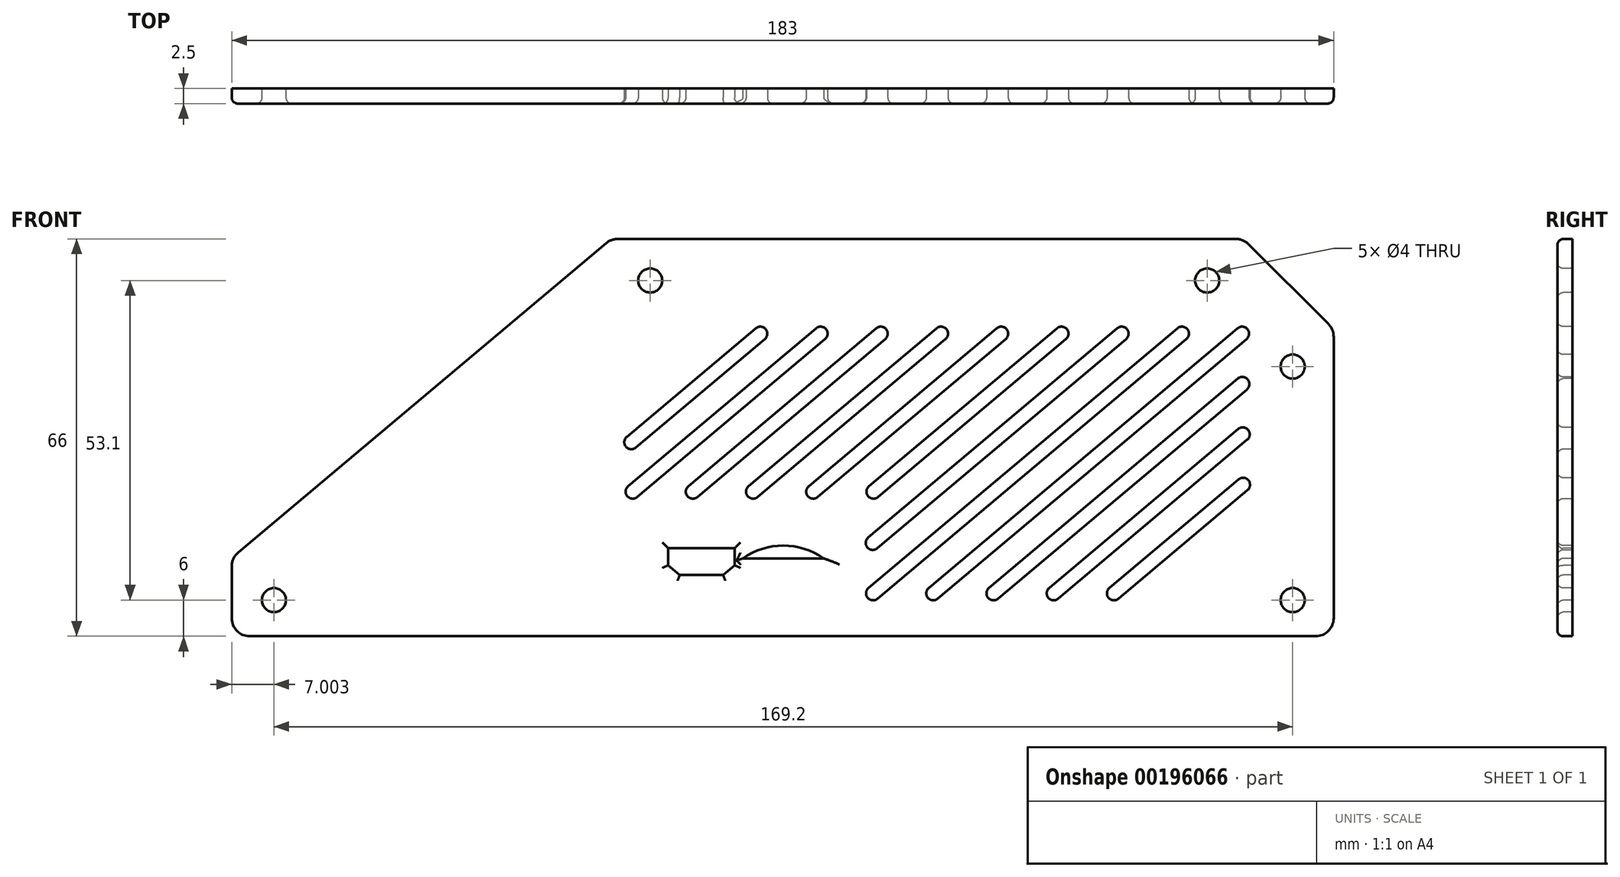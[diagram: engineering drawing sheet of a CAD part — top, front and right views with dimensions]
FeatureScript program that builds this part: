
annotation { "Feature Type Name" : "Feature", "Feature Type Description" : "" }
export const myFeature = defineFeature(function(context is Context, id is Id, definition is map)
    precondition{}
    {
        {
            var Q0;
            Q0=qCreatedBy(makeId("Front.planeOp"),FACE);
            var sketch = newSketch(context, id + "F0", { "sketchPlane" : qUnion([Q0])});
            skLineSegment(sketch, "E0.bottom", {"start": v(89.36, -33) * mm, "end": v(-93.64, -33) * mm});
            skLineSegment(sketch, "E0.top", {"start": v(89.36, 33) * mm, "end": v(-93.64, 33) * mm});
            skLineSegment(sketch, "E0.left", {"start": v(89.36, -33) * mm, "end": v(89.36, 33) * mm});
            skLineSegment(sketch, "E0.right", {"start": v(-93.64, -33) * mm, "end": v(-93.64, 33) * mm});
            skPoint(sketch, "E0.middle", {"position": v(-2.14, 0) * mm});
            skLineSegment(sketch, "E1", {"start": v(89.36, 18) * mm, "end": v(74.36, 33) * mm});
            skLineSegment(sketch, "E2", {"start": v(-93.64, -20) * mm, "end": v(-30.64, 33) * mm});
            skSolve(sketch);
        }
        {
            var Q0;
            {var subQ1=sQuery(id+"F0.wireOp",EDGE,"E0.bottom");Q0=makeQuery(id+"F0.imprint","IMPRINT",FACE,{"disambiguationData":[TD([[makeQuery(id+"F0.imprint","IMPRINT",EDGE,{"derivedFrom":subQ1}),-1.0]])]});}
            extrude(context, id + "F1", {"entities" : qUnion([Q0]), "depth" : 2.5 * mm});
        }
        {
            var Q0;
            Q0=makeQuery(id+"F1.opExtrude","CAP_FACE",FACE,{"disambiguationData":[OSD([sQuery(id+"F0.wireOp",EDGE,"E0.bottom"),sQuery(id+"F0.wireOp",EDGE,"E0.top"),sQuery(id+"F0.wireOp",EDGE,"E0.left"),sQuery(id+"F0.wireOp",EDGE,"E0.right"),sQuery(id+"F0.wireOp",EDGE,"E1"),sQuery(id+"F0.wireOp",EDGE,"E2")])],"isStart":false});
            var sketch = newSketch(context, id + "F2", { "sketchPlane" : qUnion([Q0])});
            skLineSegment(sketch, "E3", {"start": v(-24.14, 26.1) * mm, "end": v(68.36, 26.1) * mm});
            skLineSegment(sketch, "E4", {"start": v(82.56, 11.8) * mm, "end": v(82.56, -27) * mm});
            skLineSegment(sketch, "E5", {"start": v(82.56, -27) * mm, "end": v(-86.64, -27) * mm});
            skCircle(sketch, "E6", {"center": v(-24.14, 26.1) * mm, "radius": 2 * mm});
            skCircle(sketch, "E7", {"center": v(68.36, 26.1) * mm, "radius": 2 * mm});
            skCircle(sketch, "E8", {"center": v(82.56, 11.8) * mm, "radius": 2 * mm});
            skCircle(sketch, "E9", {"center": v(82.56, -27) * mm, "radius": 2 * mm});
            skCircle(sketch, "E10", {"center": v(-86.64, -27) * mm, "radius": 2 * mm});
            skLineSegment(sketch, "E11.bottom", {"start": v(4.66, -22.8) * mm, "end": v(-21.14, -22.8) * mm});
            skLineSegment(sketch, "E11.top", {"start": v(4.66, -17.7) * mm, "end": v(-21.14, -17.7) * mm});
            skLineSegment(sketch, "E11.left", {"start": v(4.66, -22.8) * mm, "end": v(4.66, -17.7) * mm});
            skLineSegment(sketch, "E11.right", {"start": v(-21.14, -22.8) * mm, "end": v(-21.14, -17.7) * mm});
            skPoint(sketch, "E11.middle", {"position": v(-8.24, -20.25) * mm});
            skLineSegment(sketch, "E12.bottom", {"start": v(4.66, -22.8) * mm, "end": v(-8.76, -22.8) * mm});
            skLineSegment(sketch, "E12.top", {"start": v(4.66, -20.08) * mm, "end": v(-8.76, -20.08) * mm});
            skLineSegment(sketch, "E12.left", {"start": v(4.66, -22.8) * mm, "end": v(4.66, -20.08) * mm});
            skLineSegment(sketch, "E12.right", {"start": v(-8.76, -22.8) * mm, "end": v(-8.76, -20.08) * mm});
            skArc(sketch, "E13", {"start": v(4.66, -20.08) * mm, "mid": v(-2.05, -17.94) * mm, "end": v(-8.76, -20.08) * mm});
            skLineSegment(sketch, "E14.bottom", {"start": v(-21.14, -22.8) * mm, "end": v(-10.14, -22.8) * mm});
            skLineSegment(sketch, "E14.top", {"start": v(-21.14, -18.4) * mm, "end": v(-10.14, -18.4) * mm});
            skLineSegment(sketch, "E14.left", {"start": v(-21.14, -22.8) * mm, "end": v(-21.14, -18.4) * mm});
            skLineSegment(sketch, "E14.right", {"start": v(-10.14, -22.8) * mm, "end": v(-10.14, -18.4) * mm});
            skLineSegment(sketch, "E15", {"start": v(-21.14, -21.2) * mm, "end": v(-19.24, -22.8) * mm});
            skLineSegment(sketch, "E16", {"start": v(-10.14, -21.2) * mm, "end": v(-12.04, -22.8) * mm});
            skSolve(sketch);
        }
        {
            var Q0;
            Q0=makeQuery(id+"F2.imprint","IMPRINT",FACE,{"disambiguationData":[TD([[makeQuery(id+"F2.imprint","IMPRINT",EDGE,{"derivedFrom":sQuery(id+"F2.wireOp",EDGE,"E6")}),1.0]])]});
            var Q1;
            Q1=makeQuery(id+"F2.imprint","IMPRINT",FACE,{"disambiguationData":[TD([[makeQuery(id+"F2.imprint","IMPRINT",EDGE,{"derivedFrom":sQuery(id+"F2.wireOp",EDGE,"E7")}),1.0]])]});
            var Q2;
            Q2=makeQuery(id+"F2.imprint","IMPRINT",FACE,{"disambiguationData":[TD([[makeQuery(id+"F2.imprint","IMPRINT",EDGE,{"derivedFrom":sQuery(id+"F2.wireOp",EDGE,"E8")}),1.0]])]});
            var Q3;
            Q3=makeQuery(id+"F2.imprint","IMPRINT",FACE,{"disambiguationData":[TD([[makeQuery(id+"F2.imprint","IMPRINT",EDGE,{"derivedFrom":sQuery(id+"F2.wireOp",EDGE,"E10")}),1.0]])]});
            var Q4;
            {var subQ0=sQuery(id+"F2.wireOp",EDGE,"E5");var subQ1=sQuery(id+"F2.wireOp",EDGE,"E4");var subQ2=makeQuery(id+"F2.imprint","INTERSECT",VERTEX,{"derivedFrom":[subQ1,subQ0]});Q4=makeQuery(id+"F2.imprint","IMPRINT",FACE,{"disambiguationData":[TD([[makeQuery(id+"F2.imprint","IMPRINT",EDGE,{"disambiguationData":[TD([[subQ2,1.0]])],"derivedFrom":subQ1}),-1.0]])]});}
            var Q5;
            {var subQ0=sQuery(id+"F2.wireOp",EDGE,"E5");var subQ1=sQuery(id+"F2.wireOp",EDGE,"E4");var subQ2=makeQuery(id+"F2.imprint","INTERSECT",VERTEX,{"derivedFrom":[subQ1,subQ0]});Q5=makeQuery(id+"F2.imprint","IMPRINT",FACE,{"disambiguationData":[TD([[makeQuery(id+"F2.imprint","IMPRINT",EDGE,{"disambiguationData":[TD([[subQ2,1.0]])],"derivedFrom":subQ1}),1.0]])]});}
            var Q6;
            Q6=makeQuery(id+"F2.imprint","IMPRINT",FACE,{"disambiguationData":[TD([[makeQuery(id+"F2.imprint","IMPRINT",EDGE,{"derivedFrom":sQuery(id+"F2.wireOp",EDGE,"E12.top")}),-1.0]])]});
            var Q7;
            Q7=makeQuery(id+"F2.imprint","IMPRINT",FACE,{"disambiguationData":[TD([[makeQuery(id+"F2.imprint","IMPRINT",EDGE,{"derivedFrom":sQuery(id+"F2.wireOp",EDGE,"E12.bottom")}),-1.0]])]});
            var Q8;
            {var subQ1=sQuery(id+"F2.wireOp",EDGE,"E14.top");Q8=makeQuery(id+"F2.imprint","IMPRINT",FACE,{"disambiguationData":[TD([[makeQuery(id+"F2.imprint","IMPRINT",EDGE,{"derivedFrom":subQ1}),-1.0]])]});}
            extrude(context, id + "F3", {"entities" : qUnion([Q0, Q1, Q2, Q3, Q4, Q5, Q6, Q7, Q8]), "operationType" : NewBodyOperationType.REMOVE, "endBound" : BoundingType.THROUGH_ALL, "oppositeDirection" : true, "depth" : 25 * mm});
        }
        {
            var Q0;
            Q0=makeQuery(id+"F1.opExtrude","CAP_FACE",FACE,{"disambiguationData":[OSD([sQuery(id+"F0.wireOp",EDGE,"E0.bottom"),sQuery(id+"F0.wireOp",EDGE,"E0.top"),sQuery(id+"F0.wireOp",EDGE,"E0.left"),sQuery(id+"F0.wireOp",EDGE,"E0.right"),sQuery(id+"F0.wireOp",EDGE,"E1"),sQuery(id+"F0.wireOp",EDGE,"E2")])],"isStart":false});
            var sketch = newSketch(context, id + "F4", { "sketchPlane" : qUnion([Q0])});
            skLineSegment(sketch, "E17", {"start": v(4.9, 16.37) * mm, "end": v(-26.3, -9.88) * mm});
            skLineSegment(sketch, "E18", {"start": v(-27.81, -8.1) * mm, "end": v(3.4, 18.16) * mm});
            skArc(sketch, "E19", {"start": v(4.9, 16.37) * mm, "mid": v(5.04, 18.02) * mm, "end": v(3.4, 18.16) * mm});
            skArc(sketch, "E20", {"start": v(-27.81, -8.1) * mm, "mid": v(-27.95, -9.74) * mm, "end": v(-26.3, -9.88) * mm});
            skLineSegment(sketch, "E21.1.0.0", {"start": v(-17.81, -8.1) * mm, "end": v(13.4, 18.16) * mm});
            skLineSegment(sketch, "E21.1.0.1", {"start": v(14.9, 16.37) * mm, "end": v(-16.3, -9.88) * mm});
            skArc(sketch, "E21.1.0.2", {"start": v(14.9, 16.37) * mm, "mid": v(15.04, 18.02) * mm, "end": v(13.4, 18.16) * mm});
            skArc(sketch, "E21.1.0.3", {"start": v(-17.81, -8.1) * mm, "mid": v(-17.95, -9.74) * mm, "end": v(-16.3, -9.88) * mm});
            skLineSegment(sketch, "E21.2.0.0", {"start": v(-7.81, -8.1) * mm, "end": v(23.4, 18.16) * mm});
            skLineSegment(sketch, "E21.2.0.1", {"start": v(24.9, 16.37) * mm, "end": v(-6.3, -9.88) * mm});
            skArc(sketch, "E21.2.0.2", {"start": v(24.9, 16.37) * mm, "mid": v(25.04, 18.02) * mm, "end": v(23.4, 18.16) * mm});
            skArc(sketch, "E21.2.0.3", {"start": v(-7.81, -8.1) * mm, "mid": v(-7.95, -9.74) * mm, "end": v(-6.3, -9.88) * mm});
            skLineSegment(sketch, "E21.3.0.0", {"start": v(2.19, -8.1) * mm, "end": v(33.4, 18.16) * mm});
            skLineSegment(sketch, "E21.3.0.1", {"start": v(34.9, 16.37) * mm, "end": v(3.7, -9.88) * mm});
            skArc(sketch, "E21.3.0.2", {"start": v(34.9, 16.37) * mm, "mid": v(35.04, 18.02) * mm, "end": v(33.4, 18.16) * mm});
            skArc(sketch, "E21.3.0.3", {"start": v(2.19, -8.1) * mm, "mid": v(2.05, -9.74) * mm, "end": v(3.7, -9.88) * mm});
            skLineSegment(sketch, "E21.4.0.0", {"start": v(12.19, -8.1) * mm, "end": v(43.4, 18.16) * mm});
            skLineSegment(sketch, "E21.4.0.1", {"start": v(44.9, 16.37) * mm, "end": v(13.7, -9.88) * mm});
            skArc(sketch, "E21.4.0.2", {"start": v(44.9, 16.37) * mm, "mid": v(45.04, 18.02) * mm, "end": v(43.4, 18.16) * mm});
            skArc(sketch, "E21.4.0.3", {"start": v(12.19, -8.1) * mm, "mid": v(12.05, -9.74) * mm, "end": v(13.7, -9.88) * mm});
            skLineSegment(sketch, "E21.direction1", {"start": v(-26.3, -9.88) * mm, "end": v(-16.3, -9.88) * mm, "construction": true});
            skLineSegment(sketch, "E22.4.0.0", {"start": v(12.07, -16.6) * mm, "end": v(53.4, 18.16) * mm});
            skLineSegment(sketch, "E22.4.0.1", {"start": v(54.9, 16.37) * mm, "end": v(13.58, -18.4) * mm});
            skArc(sketch, "E22.4.0.3", {"start": v(12.07, -16.6) * mm, "mid": v(11.93, -18.25) * mm, "end": v(13.58, -18.4) * mm});
            skArc(sketch, "E23", {"start": v(54.9, 16.37) * mm, "mid": v(55.04, 18.02) * mm, "end": v(53.4, 18.16) * mm});
            skLineSegment(sketch, "E24.1.0.0", {"start": v(12.12, -24.97) * mm, "end": v(63.4, 18.16) * mm});
            skLineSegment(sketch, "E24.1.0.1", {"start": v(64.9, 16.37) * mm, "end": v(13.63, -26.76) * mm});
            skArc(sketch, "E24.1.0.2", {"start": v(12.12, -24.97) * mm, "mid": v(11.98, -26.62) * mm, "end": v(13.63, -26.76) * mm});
            skLineSegment(sketch, "E24.2.0.0", {"start": v(22.12, -24.97) * mm, "end": v(73.4, 18.16) * mm});
            skLineSegment(sketch, "E24.2.0.1", {"start": v(74.9, 16.37) * mm, "end": v(23.63, -26.76) * mm});
            skArc(sketch, "E24.2.0.2", {"start": v(22.12, -24.97) * mm, "mid": v(21.98, -26.62) * mm, "end": v(23.63, -26.76) * mm});
            skLineSegment(sketch, "E24.3.0.0", {"start": v(32.12, -24.97) * mm, "end": v(73.45, 9.8) * mm});
            skLineSegment(sketch, "E24.3.0.1", {"start": v(74.95, 8) * mm, "end": v(33.63, -26.76) * mm});
            skArc(sketch, "E24.3.0.2", {"start": v(32.12, -24.97) * mm, "mid": v(31.98, -26.62) * mm, "end": v(33.63, -26.76) * mm});
            skLineSegment(sketch, "E24.4.0.0", {"start": v(42.12, -24.97) * mm, "end": v(73.5, 1.42) * mm});
            skLineSegment(sketch, "E24.4.0.1", {"start": v(75, -0.37) * mm, "end": v(43.63, -26.76) * mm});
            skArc(sketch, "E24.4.0.2", {"start": v(42.12, -24.97) * mm, "mid": v(41.98, -26.62) * mm, "end": v(43.63, -26.76) * mm});
            skLineSegment(sketch, "E24.5.0.0", {"start": v(52.12, -24.97) * mm, "end": v(73.55, -6.95) * mm});
            skLineSegment(sketch, "E24.5.0.1", {"start": v(75.06, -8.73) * mm, "end": v(53.63, -26.76) * mm});
            skArc(sketch, "E24.5.0.2", {"start": v(52.12, -24.97) * mm, "mid": v(51.98, -26.62) * mm, "end": v(53.63, -26.76) * mm});
            skLineSegment(sketch, "E24.6.0.0", {"start": v(-28.03, 0.14) * mm, "end": v(-6.6, 18.16) * mm});
            skLineSegment(sketch, "E24.6.0.1", {"start": v(-5.1, 16.37) * mm, "end": v(-26.53, -1.65) * mm});
            skArc(sketch, "E24.6.0.2", {"start": v(-28.03, 0.14) * mm, "mid": v(-28.17, -1.51) * mm, "end": v(-26.53, -1.65) * mm});
            skArc(sketch, "E25", {"start": v(64.9, 16.37) * mm, "mid": v(65.04, 18.02) * mm, "end": v(63.4, 18.16) * mm});
            skArc(sketch, "E26", {"start": v(74.9, 16.37) * mm, "mid": v(75.04, 18.02) * mm, "end": v(73.4, 18.16) * mm});
            skArc(sketch, "E27", {"start": v(-5.1, 16.37) * mm, "mid": v(-4.96, 18.02) * mm, "end": v(-6.6, 18.16) * mm});
            skArc(sketch, "E28", {"start": v(74.95, 8) * mm, "mid": v(75.1, 9.65) * mm, "end": v(73.45, 9.8) * mm});
            skArc(sketch, "E29", {"start": v(75, -0.37) * mm, "mid": v(75.15, 1.28) * mm, "end": v(73.5, 1.42) * mm});
            skArc(sketch, "E30", {"start": v(75.06, -8.73) * mm, "mid": v(75.2, -7.09) * mm, "end": v(73.55, -6.95) * mm});
            skSolve(sketch);
        }
        {
            var Q0;
            Q0 = qSketchRegion(id + "F4", true);
            extrude(context, id + "F5", {"entities" : qUnion([Q0]), "operationType" : NewBodyOperationType.REMOVE, "endBound" : BoundingType.THROUGH_ALL, "oppositeDirection" : true, "depth" : 25 * mm});
        }
        {
            var Q0;
            Q0=makeQuery(id+"F1.opExtrude","CAP_FACE",FACE,{"disambiguationData":[OSD([sQuery(id+"F0.wireOp",EDGE,"E0.bottom"),sQuery(id+"F0.wireOp",EDGE,"E0.top"),sQuery(id+"F0.wireOp",EDGE,"E0.left"),sQuery(id+"F0.wireOp",EDGE,"E0.right"),sQuery(id+"F0.wireOp",EDGE,"E1"),sQuery(id+"F0.wireOp",EDGE,"E2")])],"isStart":false});
            fillet(context, id + "F6", {"entities" : qUnion([Q0]), "radius" : 1 * mm, "tangentPropagation" : true, "allowEdgeOverflow" : false});
        }
        {
            var Q0;
            Q0=makeQuery(id+"F1.opExtrude","SWEPT_EDGE",EDGE,{"disambiguationData":[OSD([sQuery(id+"F0.wireOp",EDGE,"E0.bottom"),sQuery(id+"F0.wireOp",EDGE,"E0.right")])]});
            var Q1;
            Q1=makeQuery(id+"F1.opExtrude","SWEPT_EDGE",EDGE,{"disambiguationData":[OSD([sQuery(id+"F0.wireOp",EDGE,"E0.right"),sQuery(id+"F0.wireOp",EDGE,"E2")])]});
            var Q2;
            Q2=makeQuery(id+"F1.opExtrude","SWEPT_EDGE",EDGE,{"disambiguationData":[OSD([sQuery(id+"F0.wireOp",EDGE,"E0.top"),sQuery(id+"F0.wireOp",EDGE,"E2")])]});
            var Q3;
            Q3=makeQuery(id+"F1.opExtrude","SWEPT_EDGE",EDGE,{"disambiguationData":[OSD([sQuery(id+"F0.wireOp",EDGE,"E0.top"),sQuery(id+"F0.wireOp",EDGE,"E1")])]});
            var Q4;
            Q4=makeQuery(id+"F1.opExtrude","SWEPT_EDGE",EDGE,{"disambiguationData":[OSD([sQuery(id+"F0.wireOp",EDGE,"E0.left"),sQuery(id+"F0.wireOp",EDGE,"E1")])]});
            var Q5;
            Q5=makeQuery(id+"F1.opExtrude","SWEPT_EDGE",EDGE,{"disambiguationData":[OSD([sQuery(id+"F0.wireOp",EDGE,"E0.bottom"),sQuery(id+"F0.wireOp",EDGE,"E0.left")])]});
            fillet(context, id + "F7", {"entities" : qUnion([Q0, Q1, Q2, Q3, Q4, Q5]), "radius" : 3 * mm, "tangentPropagation" : true, "allowEdgeOverflow" : false});
        }
    });
